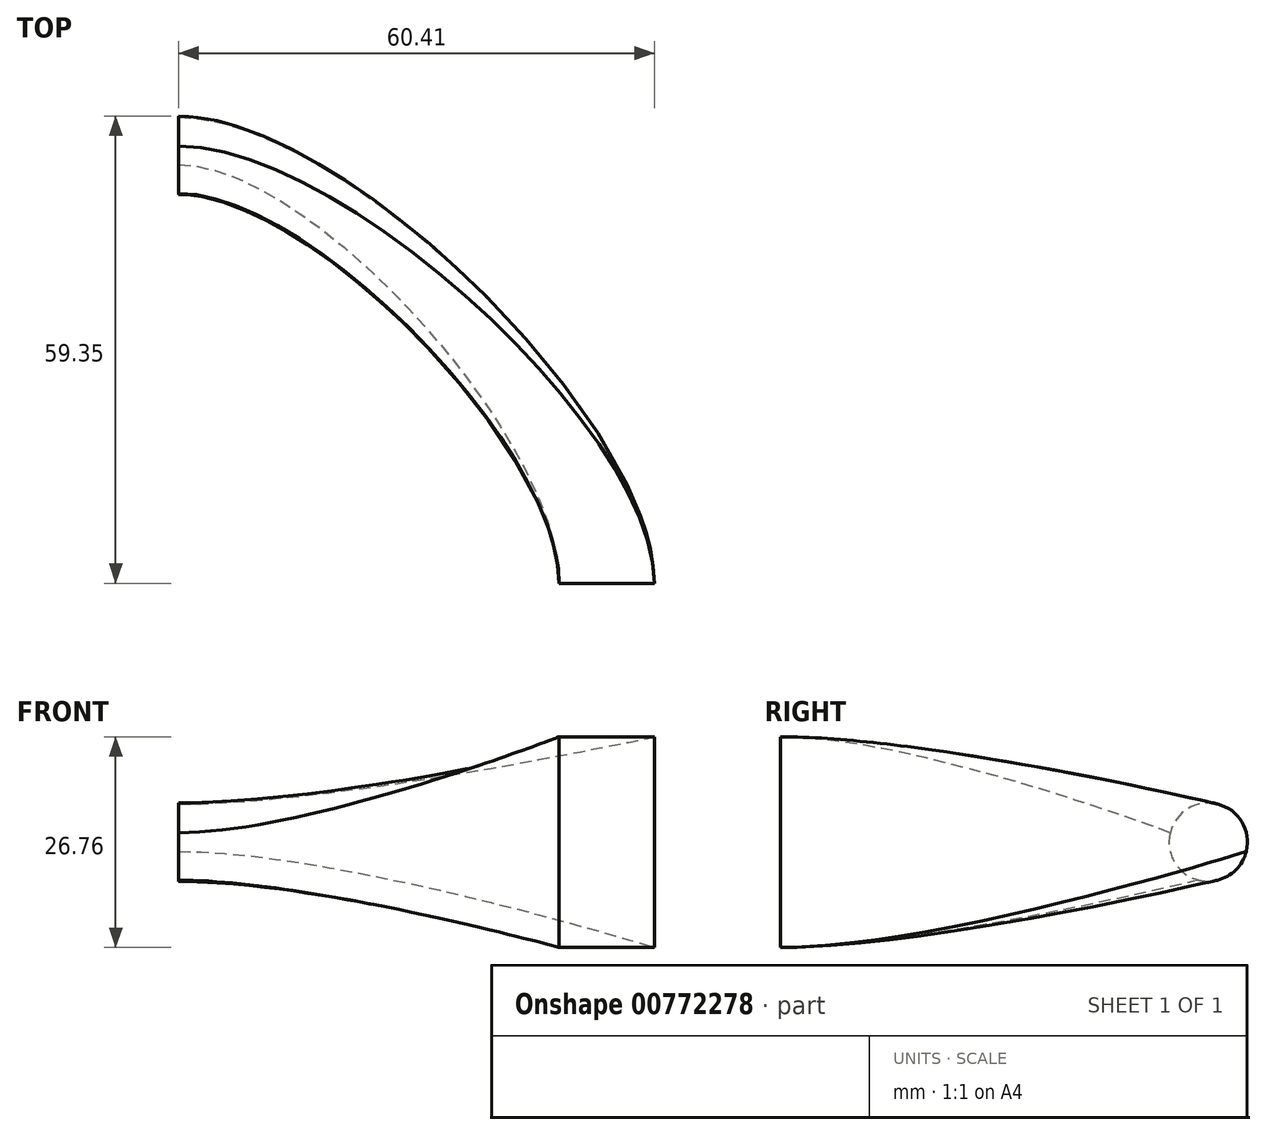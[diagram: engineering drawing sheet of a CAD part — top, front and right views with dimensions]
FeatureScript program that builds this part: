
annotation { "Feature Type Name" : "Feature", "Feature Type Description" : "" }
export const myFeature = defineFeature(function(context is Context, id is Id, definition is map)
    precondition{}
    {
        {
            var Q0;
            Q0=qCreatedBy(makeId("Top.planeOp"),FACE);
            var sketch = newSketch(context, id + "F0", { "sketchPlane" : qUnion([Q0])});
            skArc(sketch, "E0", {"start": v(54.37, 0) * mm, "mid": v(38.44, 38.44) * mm, "end": v(0, 54.37) * mm});
            skLineSegment(sketch, "E1", {"start": v(0, 69.07) * mm, "end": v(0, -62.87) * mm});
            skLineSegment(sketch, "E2", {"start": v(66, 0) * mm, "end": v(-65.34, 0) * mm});
            skSolve(sketch);
        }
        {
            var Q0;
            Q0=qCreatedBy(makeId("Front.planeOp"),FACE);
            var sketch = newSketch(context, id + "F1", { "sketchPlane" : qUnion([Q0])});
            skLineSegment(sketch, "E3.bottom", {"start": v(60.41, 13.38) * mm, "end": v(48.32, 13.38) * mm});
            skLineSegment(sketch, "E3.top", {"start": v(60.41, -13.38) * mm, "end": v(48.32, -13.38) * mm});
            skLineSegment(sketch, "E3.left", {"start": v(60.41, 13.38) * mm, "end": v(60.41, -13.38) * mm});
            skLineSegment(sketch, "E3.right", {"start": v(48.32, 13.38) * mm, "end": v(48.32, -13.38) * mm});
            skPoint(sketch, "E3.middle", {"position": v(54.37, 0) * mm});
            skSolve(sketch);
        }
        {
            var Q0;
            Q0=qCreatedBy(makeId("Right.planeOp"),FACE);
            var sketch = newSketch(context, id + "F2", { "sketchPlane" : qUnion([Q0])});
            skCircle(sketch, "E4", {"center": v(54.37, 0) * mm, "radius": 4.98 * mm});
            skSolve(sketch);
        }
        {
            var Q0;
            Q0=makeQuery(id+"F2.imprint","IMPRINT",FACE,{"disambiguationData":[TD([[makeQuery(id+"F2.imprint","IMPRINT",EDGE,{"derivedFrom":sQuery(id+"F2.wireOp",EDGE,"E4")}),1.0]])]});
            var Q1;
            Q1=makeQuery(id+"F1.imprint","IMPRINT",FACE,{"disambiguationData":[TD([[makeQuery(id+"F1.imprint","IMPRINT",EDGE,{"derivedFrom":sQuery(id+"F1.wireOp",EDGE,"E3.bottom")}),1.0]])]});
            loft(context, id + "F3", {"startCondition" : LoftEndDerivativeType.NORMAL_TO_PROFILE, "startMagnitude" : 1, "endCondition" : LoftEndDerivativeType.NORMAL_TO_PROFILE, "endMagnitude" : 1, "sheetProfilesArray" : [{ "sheetProfileEntities" : qUnion([Q0]) }, { "sheetProfileEntities" : qUnion([Q1]) }]});
        }
    });
